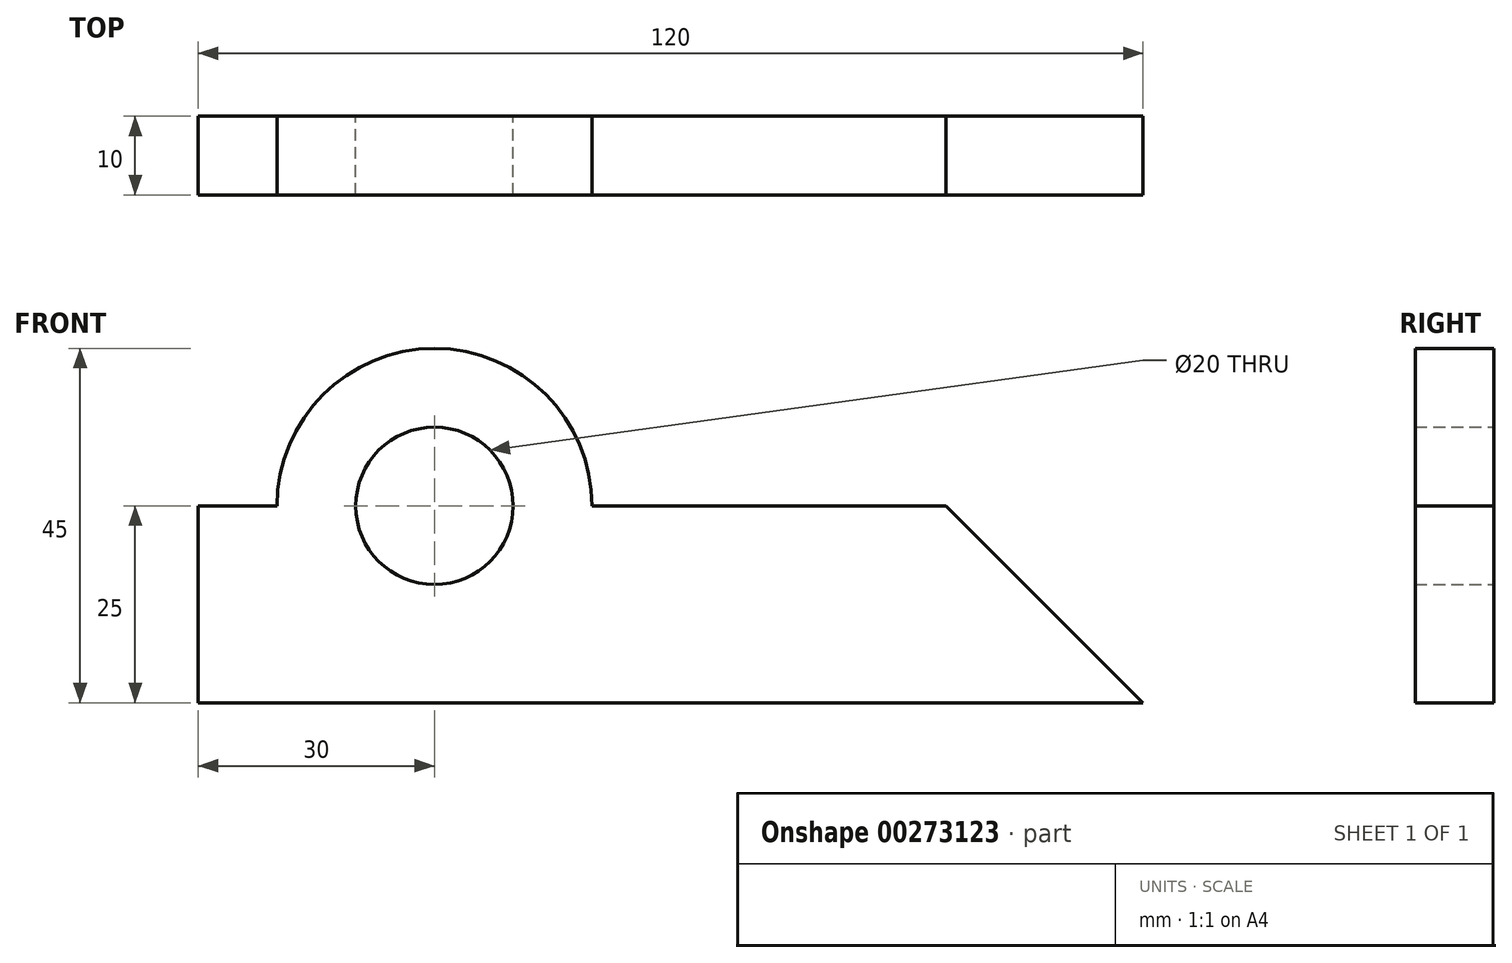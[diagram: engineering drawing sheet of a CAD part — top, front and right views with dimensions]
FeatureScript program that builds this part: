
annotation { "Feature Type Name" : "Feature", "Feature Type Description" : "" }
export const myFeature = defineFeature(function(context is Context, id is Id, definition is map)
    precondition{}
    {
        {
            var Q0;
            Q0=qCreatedBy(makeId("Front.planeOp"),FACE);
            var sketch = newSketch(context, id + "F0", { "sketchPlane" : qUnion([Q0])});
            skLineSegment(sketch, "E0", {"start": v(0, 0) * mm, "end": v(120, 0) * mm});
            skLineSegment(sketch, "E1", {"start": v(0, 0) * mm, "end": v(0, 25) * mm});
            skCircle(sketch, "E2", {"center": v(30, 25) * mm, "radius": 10 * mm});
            skLineSegment(sketch, "E3", {"start": v(0, 25) * mm, "end": v(10, 25) * mm});
            skArc(sketch, "E4", {"start": v(50, 25) * mm, "mid": v(30, 45) * mm, "end": v(10, 25) * mm});
            skLineSegment(sketch, "E5", {"start": v(120, 0) * mm, "end": v(95, 25) * mm});
            skLineSegment(sketch, "E6", {"start": v(50, 25) * mm, "end": v(95, 25) * mm});
            skSolve(sketch);
        }
        {
            var Q0;
            Q0=makeQuery(id+"F0.imprint","IMPRINT",FACE,{"disambiguationData":[TD([[makeQuery(id+"F0.imprint","IMPRINT",EDGE,{"derivedFrom":sQuery(id+"F0.wireOp",EDGE,"E0")}),1.0]])]});
            var Q1;
            Q1 = qSketchRegion(id + "F0", true);
            extrude(context, id + "F1", {"entities" : qUnion([Q0, Q1]), "depth" : 10 * mm});
        }
    });
